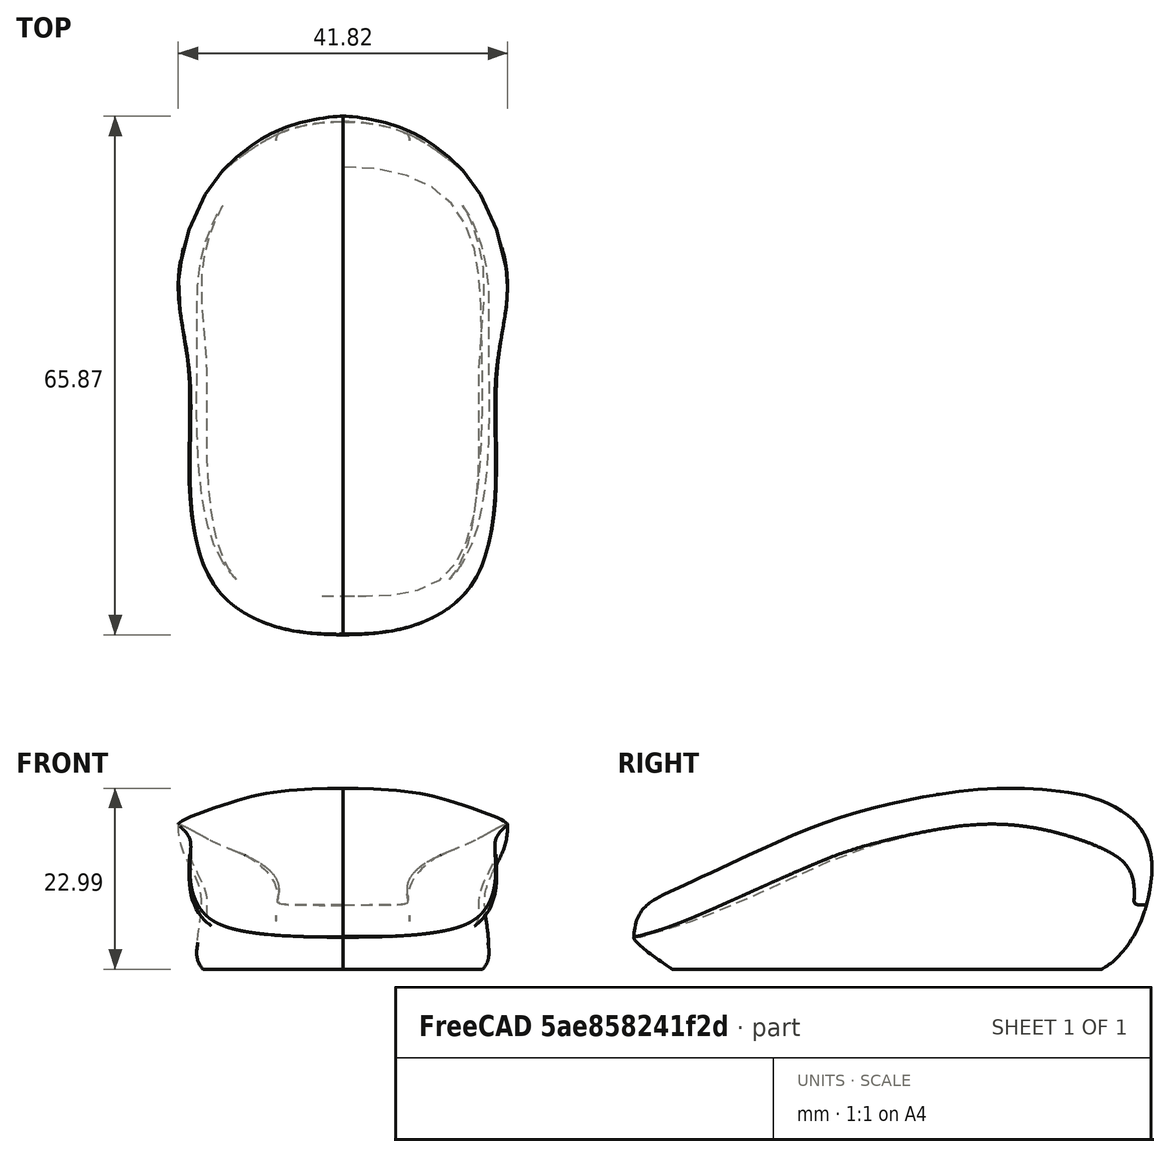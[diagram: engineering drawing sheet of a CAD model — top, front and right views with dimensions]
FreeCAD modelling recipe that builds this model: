
FCSTD DOCUMENT  (FreeCAD 1.0R39285 (Git))
Label: mouse_(unfinished)
License: All rights reserved
LicenseURL: https://en.wikipedia.org/wiki/All_rights_reserved
objects: Part::FeaturePython×15, Sketcher::SketchObject×8, Image::ImagePlane×2, PartDesign::Body×1, Part::Mirroring×1, Part::RuledSurface×1, Part::Feature×1
note: 35 computed .brp shape members not serialized (recipe doc carries the construction recipe); baked Part::Feature solids carry a one-line shape summary decoded from their .brp

FEATURE [Image::ImagePlane] ai_mouse_side  label="ai-mouse-side"
  Placement = pos=(2.7e-15,0,12) rot=(-0.707107,0,-0.707107;3.14159rad)
  XSize = 31.4299
  YSize = 68
  expr: XSize = 35.22 / 76.2 * YSize
FEATURE [Image::ImagePlane] ai_mouse_top  label="ai-mouse-top"
  Placement = pos=(0,0,0) rot=(0,0,1;3.14159rad)
  XSize = 43.9769
  YSize = 68
  expr: XSize = 49.28 / 76.2 * YSize
FEATURE [Sketcher::SketchObject] Sketch
  ArcFitTolerance = 1e-06
  AttachmentSupport = -> [XY_Plane]
  FullyConstrained = false
  MakeInternals = false
  MapMode = 5
  sketch-geometry (25):
    g0-g12: Circle [constr] x13 (B-spline internal-alignment scaffolding for g13; pole/knot coordinates omitted)
    g13: BSplineCurve PolesCount=13 KnotsCount=11 Degree=3 IsPeriodic=0
    g14-g24: GeomPoint [constr] x11 (B-spline internal-alignment scaffolding for g13; pole/knot coordinates omitted)
  constraints (8):
    c: Weight(g0) = 1
    c: Equal(g0, g1-g12) x12
    c: InternalAlignment(g0-g12 -> g13) x13
    c: InternalAlignment(g14-g24 -> g13) x11
    c: PointOnObject(g0,g-2)
    c: PointOnObject(g12,g-2)
    c: Horizontal(g13,g1)
    c: Horizontal(g13,g11)
FEATURE [Sketcher::SketchObject] Sketch001
  ArcFitTolerance = 1e-06
  AttachmentSupport = -> [YZ_Plane]
  ExternalGeometry = -> [Sketch]
  FullyConstrained = false
  MakeInternals = false
  MapMode = 5
  Placement = pos=(0,0,0) rot=(0.57735,0.57735,0.57735;2.0944rad)
  sketch-geometry (27):
    g0: LineSegment [constr] StartX=-32.3128 StartY=0 StartZ=0 EndX=-32.3128 EndY=17.5502 EndZ=0
    g1: LineSegment [constr] StartX=32.8639 StartY=0 StartZ=0 EndX=32.8639 EndY=16.819 EndZ=0
    g2-g14: Circle [constr] x13 (B-spline internal-alignment scaffolding for g15; pole/knot coordinates omitted)
    g15: BSplineCurve PolesCount=13 KnotsCount=11 Degree=3 IsPeriodic=0
    g16-g26: GeomPoint [constr] x11 (B-spline internal-alignment scaffolding for g15; pole/knot coordinates omitted)
  constraints (11):
    c: Coincident(g0,g-3)
    c: Vertical(g0)
    c: Coincident(g1,g-3)
    c: Vertical(g1)
    c: Weight(g2) = 1
    c: Equal(g2, g3-g14) x12
    c: InternalAlignment(g2-g14 -> g15) x13
    c: InternalAlignment(g16-g26 -> g15) x11
    c: PointOnObject(g3,g0)
    c: Horizontal(g13,g15)
    c: Coincident(g13,g12)
FEATURE [PartDesign::Body] Body
  AllowCompound = false
  Group = -> [Sketch,Sketch001]
  Origin = -> Origin
FEATURE [Part::FeaturePython] Mixed_curve  # WARN: FeaturePython — macro-defined, semantics opaque (R4)
  Active = false
  ApproxTolerance = 0.001
  Continuity = 5
  DegreeMax = 5
  DegreeMin = 3
  Direction1 = (0,0,0)
  Direction2 = (0,0,0)
  FillFace1 = false
  FillFace2 = false
  Parametrization = 0
  Samples = 100
  Shape1 = -> Sketch
  Shape2 = -> Sketch001
FEATURE [Sketcher::SketchObject] Sketch002
  ArcFitTolerance = 1e-06
  FullyConstrained = false
  MakeInternals = false
  Placement = pos=(0,0,0) rot=(0.57735,0.57735,0.57735;2.0944rad)
  sketch-geometry (37):
    g0-g3: Circle [constr] x4 (B-spline internal-alignment scaffolding for g4; pole/knot coordinates omitted)
    g4: BSplineCurve PolesCount=4 KnotsCount=2 Degree=3 IsPeriodic=0
    g5: GeomPoint [constr] X=-27.3642 Y=0 Z=0
    g6: GeomPoint [constr] X=-32.2199 Y=4.15583 Z=0
    g7-g16: Circle [constr] x10 (B-spline internal-alignment scaffolding for g17; pole/knot coordinates omitted)
    g17: BSplineCurve PolesCount=10 KnotsCount=8 Degree=3 IsPeriodic=0
    g18-g25: GeomPoint [constr] x8 (B-spline internal-alignment scaffolding for g17; pole/knot coordinates omitted)
    g26-g29: Circle [constr] x4 (B-spline internal-alignment scaffolding for g30; pole/knot coordinates omitted)
    g30: BSplineCurve PolesCount=4 KnotsCount=2 Degree=3 IsPeriodic=0
    g31: GeomPoint [constr] X=32.8469 Y=8.13446 Z=0
    g32: GeomPoint [constr] X=27.1324 Y=0 Z=0
    g33: LineSegment [constr] StartX=-32.2199 StartY=7.76775 StartZ=0 EndX=-32.2199 EndY=4.15583 EndZ=0
    g34: LineSegment [constr] StartX=-32.2199 StartY=4.15583 StartZ=0 EndX=-32.2199 EndY=3.30705 EndZ=0
    g35: LineSegment [constr] StartX=34.7394 StartY=15.0665 StartZ=0 EndX=32.8469 EndY=8.13446 EndZ=0
    g36: LineSegment [constr] StartX=32.8469 StartY=8.13446 StartZ=0 EndX=31.4352 EndY=2.96336 EndZ=0
  constraints (33):
    c: Weight(g0) = 1
    c: Equal(g0,g1)
    c: Equal(g0,g2)
    c: Equal(g0,g3)
    c: InternalAlignment(g0-g3 -> g4) x4
    c: InternalAlignment(g5,g4)
    c: InternalAlignment(g6,g4)
    c: PointOnObject(g0,g-1)
    c: Weight(g7) = 1
    c: Equal(g7, g8-g16) x9
    c: InternalAlignment(g7-g16 -> g17) x10
    c: InternalAlignment(g18-g25 -> g17) x8
    c: Coincident(g7,g4)
    c: Weight(g26) = 1
    c: Equal(g26,g27)
    c: Equal(g26,g28)
    c: Equal(g26,g29)
    c: InternalAlignment(g26-g29 -> g30) x4
    c: InternalAlignment(g31,g30)
    c: InternalAlignment(g32,g30)
    c: Coincident(g26,g17)
    c: PointOnObject(g29,g-1)
    c: Coincident(g33,g8)
    c: Coincident(g33,g17)
    c: Vertical(g33)
    c: Coincident(g34,g17)
    c: Coincident(g34,g2)
    c: Parallel(g33,g34)
    c: Coincident(g35,g15)
    c: Coincident(g35,g30)
    c: Coincident(g36,g17)
    c: Coincident(g36,g27)
    c: Parallel(g35,g36)
FEATURE [Sketcher::SketchObject] Sketch003
  ArcFitTolerance = 1e-06
  ExternalGeometry = -> [Sketch002]
  FullyConstrained = false
  MakeInternals = false
  sketch-geometry (13):
    g0-g6: Circle [constr] x7 (B-spline internal-alignment scaffolding for g7; pole/knot coordinates omitted)
    g7: BSplineCurve PolesCount=7 KnotsCount=5 Degree=3 IsPeriodic=0
    g8-g12: GeomPoint [constr] x5 (B-spline internal-alignment scaffolding for g7; pole/knot coordinates omitted)
  constraints (8):
    c: Weight(g0) = 1
    c: Equal(g0, g1-g6) x6
    c: InternalAlignment(g0-g6 -> g7) x7
    c: InternalAlignment(g8-g12 -> g7) x5
    c: Coincident(g0,g-3)
    c: Coincident(g6,g-4)
    c: Horizontal(g7,g1)
    c: Horizontal(g7,g5)
FEATURE [Part::FeaturePython] Freehand_BSpline001  # WARN: FeaturePython — macro-defined, semantics opaque (R4)
  Data = (5) [(20.8383,13.5717,18.4364),(20.6284,13.5939,16.1845),(18.0294,13.6164,9.56747),(17.8393,13.6388,0.970634),(17.2442,13.661,0)]
  DataType = [1,0,0,0,1]
  Parametrization = 1
  Periodic = false
  Support = -> [Mixed_curve,Sketch003]
  Tangents = (5) [(0,0,0),(0,0,0),(0,0,0),(0,0,0),(0,0,0)]
  Tolerance = 1e-07
FEATURE [Part::FeaturePython] JoinCurve  # WARN: FeaturePython — macro-defined, semantics opaque (R4)
  Active = false
  ApproxTolerance = 0.001
  Continuity = 5
  CornerBreak = false
  DegreeMax = 5
  DegreeMin = 3
  Edges = -> [Sketch002]
  ForceClosed = false
  ForceContact = true
  Parametrization = 0
  Reverse = false
  Samples = 100
  StartOffset = 0
  Tolerance = 0.01
FEATURE [Part::FeaturePython] JoinCurve001  # WARN: FeaturePython — macro-defined, semantics opaque (R4)
  Active = false
  ApproxTolerance = 0.001
  Continuity = 5
  CornerBreak = false
  DegreeMax = 5
  DegreeMin = 3
  Edges = -> [Sketch002]
  ForceClosed = false
  ForceContact = true
  Parametrization = 0
  Reverse = false
  Samples = 100
  StartOffset = 0
  Tolerance = 0.01
FEATURE [Part::FeaturePython] JoinCurve002  # WARN: FeaturePython — macro-defined, semantics opaque (R4)
  Active = false
  ApproxTolerance = 0.001
  Continuity = 5
  CornerBreak = false
  DegreeMax = 5
  DegreeMin = 3
  Edges = -> [Sketch003]
  ForceClosed = false
  ForceContact = true
  Parametrization = 0
  Reverse = false
  Samples = 100
  StartOffset = 0
  Tolerance = 0.01
FEATURE [Part::FeaturePython] Gordon  # WARN: FeaturePython — macro-defined, semantics opaque (R4)
  FlipNormal = false
  MaxCtrlPts = 80
  Output = 0
  SamplesU = 16
  SamplesV = 16
  Sources = -> [Mixed_curve,JoinCurve002,JoinCurve,Freehand_BSpline001,JoinCurve001]
  Tol2D = 1e-05
  Tol3D = 0.01
FEATURE [Part::FeaturePython] Freehand_BSpline  # WARN: FeaturePython — macro-defined, semantics opaque (R4)
  Data = (2) [(15.6834,-26.8658,5.72958),(0,-29.4662,8.94748)]
  DataType = [1,1]
  Parametrization = 1
  Periodic = false
  Support = -> [Mixed_curve,Sketch002]
  Tangents = (2) [(0,0,0),(0,0,0)]
  Tolerance = 1e-07
FEATURE [Part::FeaturePython] Freehand_BSpline002  # WARN: FeaturePython — macro-defined, semantics opaque (R4)
  Data = (2) [(20.7291,14.5341,18.4114),(0,14.9584,22.9825)]
  DataType = [1,1]
  Parametrization = 1
  Periodic = false
  Support = -> [Mixed_curve,Sketch002]
  Tangents = (2) [(0,0,0),(0,0,0)]
  Tolerance = 1e-07
FEATURE [Part::FeaturePython] Freehand_BSpline003  # WARN: FeaturePython — macro-defined, semantics opaque (R4)
  Data = (2) [(14.5586,27.1531,15.3747),(0,31.1928,18.9406)]
  DataType = [1,1]
  Parametrization = 1
  Periodic = false
  Support = -> [Mixed_curve,Sketch002]
  Tangents = (2) [(0,0,0),(0,0,0)]
  Tolerance = 1e-07
FEATURE [Sketcher::SketchObject] Sketch004
  ArcFitTolerance = 1e-06
  ExternalGeometry = -> [Freehand_BSpline,Freehand_BSpline002,Freehand_BSpline003]
  FullyConstrained = true
  MakeInternals = false
  Placement = pos=(0,0,0) rot=(0.57735,0.57735,0.57735;2.0944rad)
  sketch-geometry (3):
    g0: LineSegment StartX=-29.4662 StartY=8.94748 StartZ=0 EndX=-26.8658 EndY=5.72958 EndZ=0
    g1: LineSegment StartX=14.9584 StartY=22.9825 StartZ=0 EndX=14.5341 EndY=18.4114 EndZ=0
    g2: LineSegment StartX=31.1928 StartY=18.9406 StartZ=0 EndX=27.1531 EndY=15.3747 EndZ=0
  constraints (6):
    c: Coincident(g0,g-3)
    c: Coincident(g0,g-3)
    c: Coincident(g1,g-4)
    c: Coincident(g1,g-4)
    c: Coincident(g2,g-5)
    c: Coincident(g2,g-5)
FEATURE [Sketcher::SketchObject] Sketch005
  ArcFitTolerance = 1e-06
  AttachmentSupport = -> [Freehand_BSpline,Sketch004]
  ExternalGeometry = -> [Freehand_BSpline]
  FullyConstrained = false
  MakeInternals = false
  MapMode = 13
  Placement = pos=(5.2278,-27.7326,6.80221) rot=(1,0,0;2.25046rad)
  sketch-geometry (13):
    g0-g6: Circle [constr] x7 (B-spline internal-alignment scaffolding for g7; pole/knot coordinates omitted)
    g7: BSplineCurve PolesCount=7 KnotsCount=5 Degree=3 IsPeriodic=0
    g8-g12: GeomPoint [constr] x5 (B-spline internal-alignment scaffolding for g7; pole/knot coordinates omitted)
  constraints (7):
    c: Weight(g0) = 1
    c: Equal(g0, g1-g6) x6
    c: InternalAlignment(g0-g6 -> g7) x7
    c: InternalAlignment(g8-g12 -> g7) x5
    c: Coincident(g0,g-3)
    c: Coincident(g6,g-3)
    c: Horizontal(g7,g1)
FEATURE [Sketcher::SketchObject] Sketch006
  ArcFitTolerance = 1e-06
  AttachmentSupport = -> [Freehand_BSpline002,Sketch004]
  ExternalGeometry = -> [Freehand_BSpline002]
  FullyConstrained = false
  MakeInternals = false
  MapMode = 13
  Placement = pos=(6.9097,14.6755,19.9351) rot=(1,0,0;1.47823rad)
  sketch-geometry (9):
    g0-g4: Circle [constr] x5 (B-spline internal-alignment scaffolding for g5; pole/knot coordinates omitted)
    g5: BSplineCurve PolesCount=5 KnotsCount=3 Degree=3 IsPeriodic=0
    g6: GeomPoint [constr] X=-6.9097 Y=3.06049 Z=0
    g7: GeomPoint [constr] X=6.61143 Y=1.44564 Z=0
    g8: GeomPoint [constr] X=13.8194 Y=-1.53025 Z=0
  constraints (9):
    c: Weight(g0) = 1
    c: Equal(g0, g1-g4) x4
    c: InternalAlignment(g0-g4 -> g5) x5
    c: InternalAlignment(g6,g5)
    c: InternalAlignment(g7,g5)
    c: InternalAlignment(g8,g5)
    c: Coincident(g0,g-3)
    c: Coincident(g4,g-3)
    c: Vertical(g3,g5)
FEATURE [Sketcher::SketchObject] Sketch007
  ArcFitTolerance = 1e-06
  AttachmentSupport = -> [Freehand_BSpline003,Sketch004]
  ExternalGeometry = -> [Freehand_BSpline003]
  FullyConstrained = false
  MakeInternals = false
  MapMode = 13
  Placement = pos=(4.85287,28.4996,16.5633) rot=(1,0,0;0.72318rad)
  sketch-geometry (7):
    g0-g3: Circle [constr] x4 (B-spline internal-alignment scaffolding for g4; pole/knot coordinates omitted)
    g4: BSplineCurve PolesCount=4 KnotsCount=2 Degree=3 IsPeriodic=0
    g5: GeomPoint [constr] X=-4.85287 Y=3.59229 Z=0
    g6: GeomPoint [constr] X=9.70575 Y=-1.79615 Z=0
  constraints (11):
    c: Weight(g0) = 1
    c: Equal(g0,g1)
    c: Equal(g0,g2)
    c: Equal(g0,g3)
    c: InternalAlignment(g0-g3 -> g4) x4
    c: InternalAlignment(g5,g4)
    c: InternalAlignment(g6,g4)
    c: Coincident(g0,g-3)
    c: Coincident(g3,g-3)
    c: Horizontal(g4,g1)
    c: Vertical(g2,g4)
FEATURE [Part::FeaturePython] SplitCurve  # WARN: FeaturePython — macro-defined, semantics opaque (R4)
  CutAtVertexes = false
  Distance = 0
  KeepSolid = false
  NormalizedParameters = [0,0.0964506,0.192892,0.289333,0.385774,0.481064,0.481064,0.574025,0.666127,0.756871,0.847644,1]
  Number = 10
  Source = -> Mixed_curve [Edge1]
  Values = 50.000%
FEATURE [Part::FeaturePython] JoinCurve003  # WARN: FeaturePython — macro-defined, semantics opaque (R4)
  Active = false
  ApproxTolerance = 0.001
  Continuity = 5
  CornerBreak = false
  DegreeMax = 5
  DegreeMin = 3
  Edges = -> [SplitCurve]
  ForceClosed = false
  ForceContact = true
  Parametrization = 0
  Reverse = false
  Samples = 100
  StartOffset = 0
  Tolerance = 0.01
FEATURE [Part::FeaturePython] JoinCurve004  # WARN: FeaturePython — macro-defined, semantics opaque (R4)
  Active = false
  ApproxTolerance = 0.001
  Continuity = 5
  CornerBreak = false
  DegreeMax = 5
  DegreeMin = 3
  Edges = -> [SplitCurve]
  ForceClosed = false
  ForceContact = true
  Parametrization = 0
  Reverse = false
  Samples = 100
  StartOffset = 0
  Tolerance = 0.01
FEATURE [Part::FeaturePython] JoinCurve005  # WARN: FeaturePython — macro-defined, semantics opaque (R4)
  Active = false
  ApproxTolerance = 0.001
  Continuity = 5
  CornerBreak = false
  DegreeMax = 5
  DegreeMin = 3
  Edges = -> [SplitCurve]
  ForceClosed = false
  ForceContact = true
  Parametrization = 0
  Reverse = false
  Samples = 100
  StartOffset = 0
  Tolerance = 0.01
FEATURE [Part::FeaturePython] Gordon001  # WARN: FeaturePython — macro-defined, semantics opaque (R4)
  FlipNormal = false
  MaxCtrlPts = 80
  Output = 0
  SamplesU = 16
  SamplesV = 16
  Sources = -> [JoinCurve003,Sketch002,JoinCurve004,Sketch005,Sketch006,Sketch007,JoinCurve005]
  Tol2D = 1e-05
  Tol3D = 0.01
FEATURE [Part::FeaturePython] Connect  # WARN: FeaturePython — macro-defined, semantics opaque (R4)
  Objects = -> [Gordon001,Gordon]
  Tolerance = 0
FEATURE [Part::Mirroring] Part__Mirroring  label="Connect (Mirror #1)"
  Base = (0,0,0)
  Normal = (1,0,0)
  Source = -> Connect
FEATURE [Part::RuledSurface] Ruled_Surface
  Curve1 = -> Connect [Edge68]
  Curve2 = -> Part__Mirroring [Edge68]
  Orientation = 0
FEATURE [Part::Feature] Shell
  shape: bbox 41.96 x 65.95 x 23.06 mm, 5 faces, 0 solids (baked)
